# Revit family: Ventüer_VentilationLouvres_VL-50CM
name_source: partatom
category: Generic Models
units: mm (PartAtom-declared; Revit-internal decimal feet)

## family parameters
Always vertical = No
Can host rebar = No
Cut with Voids When Loaded = No
Part Type = Normal
Room Calculation Point = No
Round Connector Dimension = Use Diameter
Shared = No
Work Plane-Based = Yes

## types (4) — shared parameters
Aerodynamic Performance = Air Inlet: 0.332, Class 2. Air Extract: 0.389, Class 2
Ancillaries = Bird Mesh, Insect Mesh, Solid Blanking, Perimeter Mounting Angle
Blade And Frame Gap = 12 mm  [stored 0.0393701 ft]
Blade Centres = 50 mm  [stored 0.164042 ft]
Blade Material = Ventüer Aluminium
Clip Height = 560 mm
Clip Multiple Transition = No
Clip Single Transition = Yes
Clip Transition Count = 3
Default Elevation = 1219 mm
Description = Minimalistic Screening Louvre
Exact Neck Height = 594 mm  [stored 1.94882 ft]
Exact Neck Height Check = 594 mm  [stored 1.94882 ft]
Exact Neck Width = 594 mm  [stored 1.94882 ft]
Exact Neck Width Check = 594 mm  [stored 1.94882 ft]
Frame Material = Ventüer Aluminium
Frame Set Count = 1
Frame Set Count Check = 2
Frame Set Transition Count = 1
Frame Set Transition Count Check = 2
Manufacturer = Ventüer
Max Flow = 5000.0 L/s
Min Flow = 100.0 L/s
Model = VL-50CM
Multiple Frame Set = No
Multiple Transition = No
Noise Level NC Max = 0.00 NC
Noise Level NC Min = 0.00 NC
Nominal Height = 600 mm
Nominal Width = 600 mm
Nominated Air Flow = 100.0 L/s
Nominated Pessure Drop = 21.0 Pa
Post Depth = 200 mm  [stored 0.656168 ft]
Post Width = 100 mm  [stored 0.328084 ft]
Rain Defence Performance = Class C - up to 1.0m/s suction velocity. Class D - up to 3.5m/s suction velocity
Rear Frame Set Offset = 19 mm
Single Transition = No
Specified Air Flow = 0.0 L/s
Specified Pressure Drop = 21.0 Pa
Static Pressure Max = 60.0 Pa
Static Pressure Min = 10.0 Pa
URL = https://www.ventuer.co
Ventüer Product Range = Ventilation Louvres

## per-type parameters (varying)
| type | Base Width | Blade Count | Blade Cut Offset | Channel | Clip | Connector Height | Connector Width | Depth | Flanged | Frame Set Height | Frame Set Width | Glazed | Keynote | Overall Opening Height | Overall Opening Width | Profile Width | Rear Mullion Offset | Single Frame Set | Single Frame Set Width | Top Blade | Top Blade Corrector | Top Blade Height |
| VL-50CM_CF | 25 mm  [stored 0.082021 ft] | 10 | 500 mm  [stored 1.64042 ft] | Yes | No | 566 mm | 566 mm | 150 mm | No | 566 mm | 588 mm | No | VL-50CM_CF | 566 mm | 566 mm | 3 mm  [stored 0.00984252 ft] | 1 mm  [stored 0.00328084 ft] | Yes | 294 mm | Yes | 0 mm  [stored 0 ft] | 54 mm |
| VL-50CM_GF | 26 mm | 10 | 500 mm  [stored 1.64042 ft] | No | No | 540 mm | 540 mm | 155 mm | No | 540 mm | 538 mm | Yes | VL-50CM_GF | 540 mm | 540 mm | 28 mm | 1 mm  [stored 0.00328084 ft] | Yes | 269 mm | Yes | 1 mm  [stored 0.00328084 ft] | 29 mm |
| VL-50CM_FF | 25 mm  [stored 0.082021 ft] | 10 | 500 mm  [stored 1.64042 ft] | No | No | 544 mm | 544 mm | 160 mm  [stored 0.524934 ft] | Yes | 544 mm | 544 mm | No | VL-50CM_FF | 544 mm | 544 mm | 25 mm  [stored 0.082021 ft] | 1 mm  [stored 0.00328084 ft] | Yes | 272 mm | Yes | 1 mm  [stored 0.00328084 ft] | 33 mm |
| VL-50CM_Clip | 0 mm  [stored 0 ft] | 11 | 550 mm | No | Yes | 594 mm  [stored 1.94882 ft] | 594 mm  [stored 1.94882 ft] | 160 mm  [stored 0.524934 ft] | No | 594 mm  [stored 1.94882 ft] | 594 mm  [stored 1.94882 ft] | No | VL-50CM_FF | 594 mm  [stored 1.94882 ft] | 594 mm  [stored 1.94882 ft] | 0 mm  [stored 0 ft] | 22 mm | No | 297 mm  [stored 0.974409 ft] | No | 1 mm  [stored 0.00328084 ft] | 33 mm |

note: [stored X ft] marks values corroborated as IEEE doubles in the binary element streams (Revit-internal decimal feet)

## geometry (parser evidence)
native form markers: Sweep x37
no freeform markers — native parametric forms only
